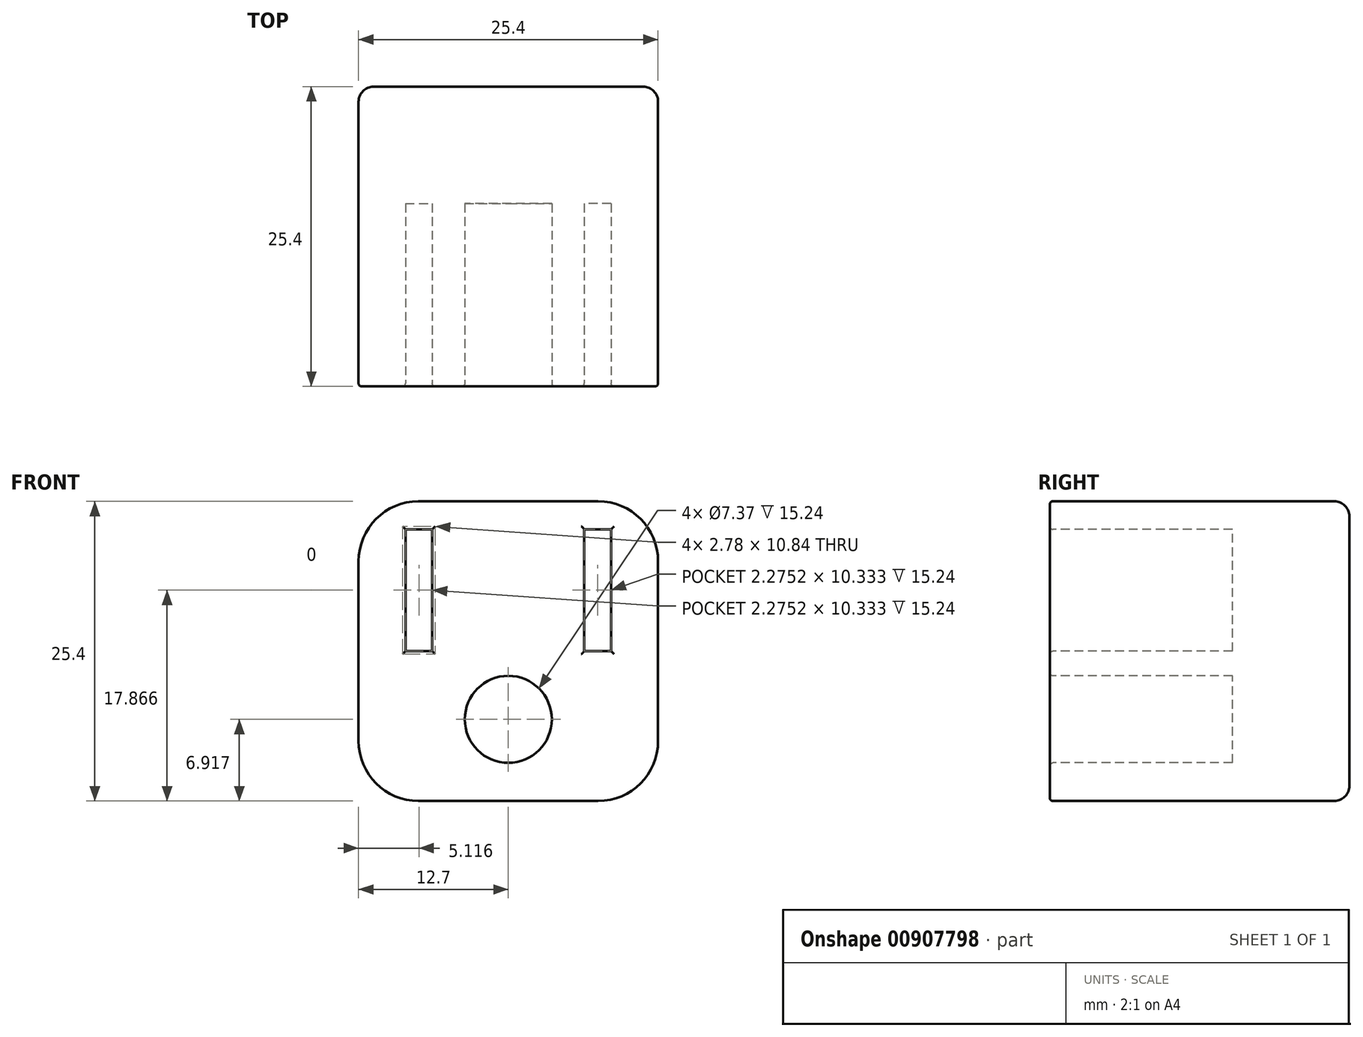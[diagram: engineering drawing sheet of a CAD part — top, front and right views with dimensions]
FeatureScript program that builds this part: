
annotation { "Feature Type Name" : "Feature", "Feature Type Description" : "" }
export const myFeature = defineFeature(function(context is Context, id is Id, definition is map)
    precondition{}
    {
        {
            var Q0;
            Q0=qCreatedBy(makeId("Front.planeOp"),FACE);
            var sketch = newSketch(context, id + "F0", { "sketchPlane" : qUnion([Q0])});
            skLineSegment(sketch, "E0.bottom", {"start": v(-12.7, 12.7) * mm, "end": v(12.7, 12.7) * mm});
            skLineSegment(sketch, "E0.top", {"start": v(-12.7, -12.7) * mm, "end": v(12.7, -12.7) * mm});
            skLineSegment(sketch, "E0.left", {"start": v(-12.7, 12.7) * mm, "end": v(-12.7, -12.7) * mm});
            skLineSegment(sketch, "E0.right", {"start": v(12.7, 12.7) * mm, "end": v(12.7, -12.7) * mm});
            skPoint(sketch, "E0.middle", {"position": v(0, 0) * mm});
            skSolve(sketch);
        }
        {
            var Q0;
            Q0 = qSketchRegion(id + "F0", true);
            extrude(context, id + "F1", {"entities" : qUnion([Q0]), "depth" : 25.4 * mm, "offsetDistance" : 25.4 * mm});
        }
        {
            var Q0;
            Q0=makeQuery(id+"F1.opExtrude","CAP_FACE",FACE,{"disambiguationData":[OSD([sQuery(id+"F0.wireOp",EDGE,"E0.bottom"),sQuery(id+"F0.wireOp",EDGE,"E0.top"),sQuery(id+"F0.wireOp",EDGE,"E0.left"),sQuery(id+"F0.wireOp",EDGE,"E0.right")])],"isStart":false});
            var sketch = newSketch(context, id + "F2", { "sketchPlane" : qUnion([Q0])});
            skLineSegment(sketch, "E1", {"start": v(0, 12.7) * mm, "end": v(0, -12.7) * mm, "construction": true});
            skLineSegment(sketch, "E2.bottom", {"start": v(-8.72, 0) * mm, "end": v(-6.45, 0) * mm});
            skLineSegment(sketch, "E2.top", {"start": v(-8.72, 10.33) * mm, "end": v(-6.45, 10.33) * mm});
            skLineSegment(sketch, "E2.left", {"start": v(-8.72, 0) * mm, "end": v(-8.72, 10.33) * mm});
            skLineSegment(sketch, "E2.right", {"start": v(-6.45, 0) * mm, "end": v(-6.45, 10.33) * mm});
            skLineSegment(sketch, "E3.MirrorCS", {"start": v(8.72, 10.33) * mm, "end": v(6.45, 10.33) * mm});
            skLineSegment(sketch, "E4.MirrorCS", {"start": v(8.72, 0) * mm, "end": v(8.72, 10.33) * mm});
            skLineSegment(sketch, "E5.MirrorCS", {"start": v(8.72, 0) * mm, "end": v(6.45, 0) * mm});
            skLineSegment(sketch, "E6.MirrorCS", {"start": v(6.45, 0) * mm, "end": v(6.45, 10.33) * mm});
            skCircle(sketch, "E7", {"center": v(0, -5.78) * mm, "radius": 3.69 * mm});
            skSolve(sketch);
        }
        {
            var Q0;
            Q0 = qSketchRegion(id + "F2", true);
            extrude(context, id + "F3", {"entities" : qUnion([Q0]), "operationType" : NewBodyOperationType.REMOVE, "oppositeDirection" : true, "depth" : 15.5 * mm, "offsetDistance" : 25.4 * mm});
        }
        {
            var Q0;
            Q0=makeQuery(id+"F1.opExtrude","SWEPT_EDGE",EDGE,{"disambiguationData":[OSD([sQuery(id+"F0.wireOp",EDGE,"E0.bottom"),sQuery(id+"F0.wireOp",EDGE,"E0.left")])]});
            var Q1;
            Q1=makeQuery(id+"F1.opExtrude","SWEPT_EDGE",EDGE,{"disambiguationData":[OSD([sQuery(id+"F0.wireOp",EDGE,"E0.bottom"),sQuery(id+"F0.wireOp",EDGE,"E0.right")])]});
            var Q2;
            Q2=makeQuery(id+"F1.opExtrude","SWEPT_EDGE",EDGE,{"disambiguationData":[OSD([sQuery(id+"F0.wireOp",EDGE,"E0.top"),sQuery(id+"F0.wireOp",EDGE,"E0.left")])]});
            var Q3;
            Q3=makeQuery(id+"F1.opExtrude","SWEPT_EDGE",EDGE,{"disambiguationData":[OSD([sQuery(id+"F0.wireOp",EDGE,"E0.top"),sQuery(id+"F0.wireOp",EDGE,"E0.right")])]});
            fillet(context, id + "F4", {"entities" : qUnion([Q0, Q1, Q2, Q3]), "radius" : 5.08 * mm, "tangentPropagation" : true, "allowEdgeOverflow" : false});
        }
        {
            var Q0;
            Q0=makeQuery(id+"F1.opExtrude","CAP_FACE",FACE,{"disambiguationData":[OSD([sQuery(id+"F0.wireOp",EDGE,"E0.bottom"),sQuery(id+"F0.wireOp",EDGE,"E0.top"),sQuery(id+"F0.wireOp",EDGE,"E0.left"),sQuery(id+"F0.wireOp",EDGE,"E0.right")])],"isStart":true});
            fillet(context, id + "F5", {"entities" : qUnion([Q0]), "radius" : 1.27 * mm, "tangentPropagation" : true, "allowEdgeOverflow" : false});
        }
        {
            var Q0;
            Q0=makeQuery(id+"F1.opExtrude","CAP_FACE",FACE,{"disambiguationData":[OSD([sQuery(id+"F0.wireOp",EDGE,"E0.bottom"),sQuery(id+"F0.wireOp",EDGE,"E0.top"),sQuery(id+"F0.wireOp",EDGE,"E0.left"),sQuery(id+"F0.wireOp",EDGE,"E0.right")])],"isStart":false});
            fillet(context, id + "F6", {"entities" : qUnion([Q0]), "radius" : 0.25 * mm, "tangentPropagation" : true, "allowEdgeOverflow" : false});
        }
    });
